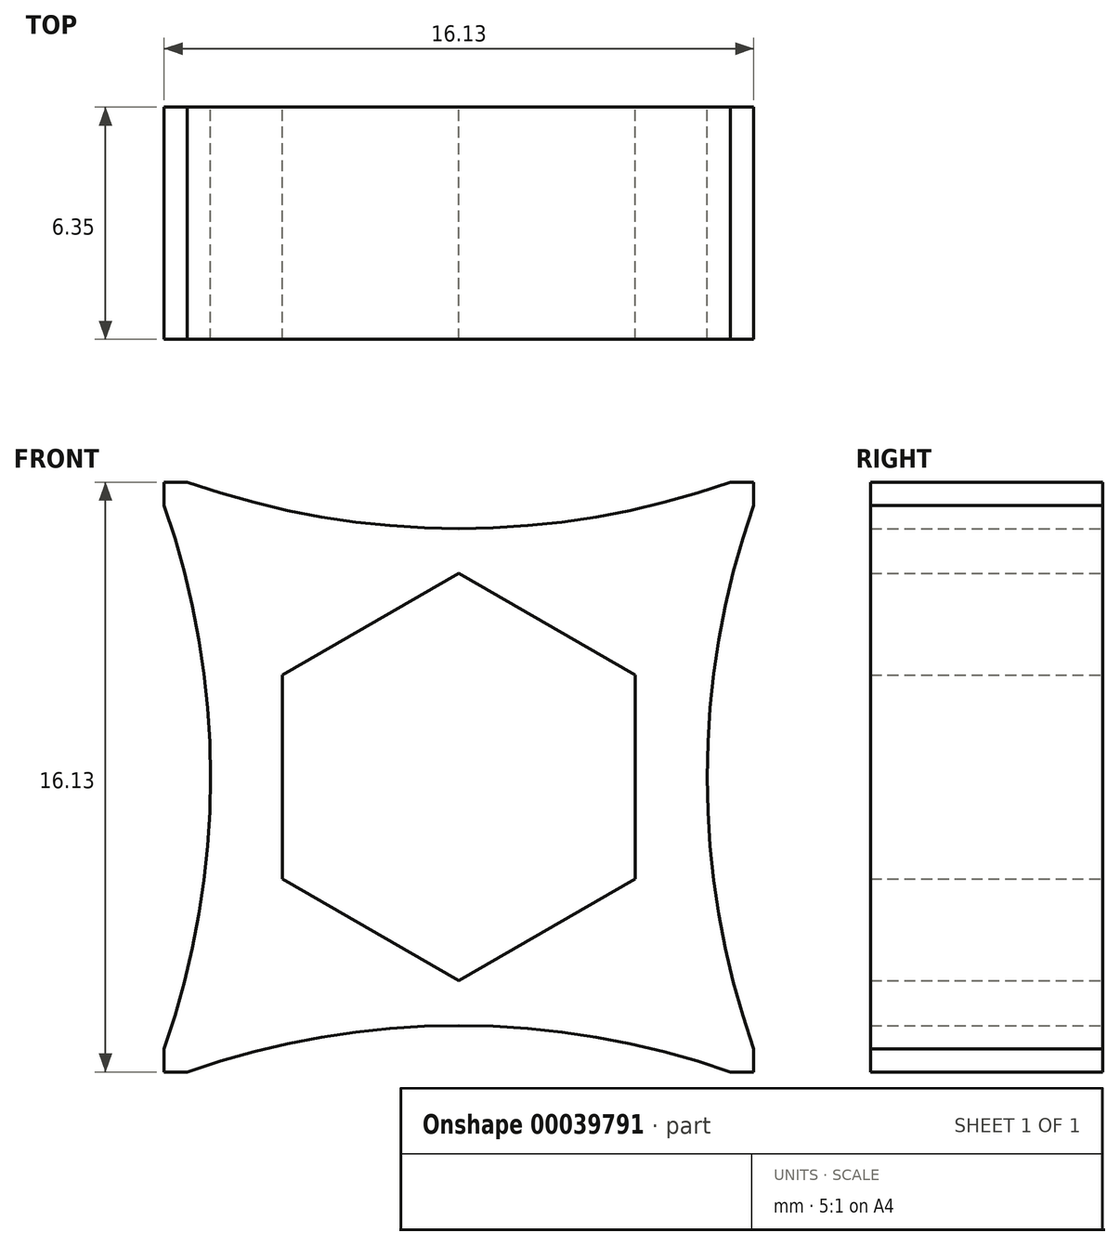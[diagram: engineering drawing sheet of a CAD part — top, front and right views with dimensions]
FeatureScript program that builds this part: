
annotation { "Feature Type Name" : "Feature", "Feature Type Description" : "" }
export const myFeature = defineFeature(function(context is Context, id is Id, definition is map)
    precondition{}
    {
        {
            var Q0;
            Q0=qCreatedBy(makeId("Front.planeOp"),FACE);
            var sketch = newSketch(context, id + "F0", { "sketchPlane" : qUnion([Q0])});
            skLineSegment(sketch, "E0", {"start": v(16.13, 16.13) * mm, "end": v(16.13, 15.5) * mm});
            skLineSegment(sketch, "E1", {"start": v(16.13, 0) * mm, "end": v(16.13, 0.64) * mm});
            skLineSegment(sketch, "E2", {"start": v(16.13, 8.06) * mm, "end": v(14.86, 8.06) * mm, "construction": true});
            skArc(sketch, "E3", {"start": v(16.13, 15.5) * mm, "mid": v(14.86, 8.06) * mm, "end": v(16.13, 0.63) * mm});
            skLineSegment(sketch, "E4", {"start": v(16.13, 16.13) * mm, "end": v(15.5, 16.13) * mm});
            skLineSegment(sketch, "E5", {"start": v(0, 16.13) * mm, "end": v(0.64, 16.13) * mm});
            skLineSegment(sketch, "E6", {"start": v(8.06, 16.13) * mm, "end": v(8.06, 14.86) * mm, "construction": true});
            skArc(sketch, "E7", {"start": v(0.64, 16.13) * mm, "mid": v(8.06, 14.86) * mm, "end": v(15.5, 16.13) * mm});
            skLineSegment(sketch, "E8", {"start": v(0, 16.13) * mm, "end": v(0, 15.5) * mm});
            skLineSegment(sketch, "E9", {"start": v(0, 0) * mm, "end": v(0, 1.27) * mm});
            skLineSegment(sketch, "E10", {"start": v(0, 8.06) * mm, "end": v(1.27, 8.06) * mm, "construction": true});
            skLineSegment(sketch, "E11", {"start": v(0, 0) * mm, "end": v(0, 0.64) * mm});
            skArc(sketch, "E12", {"start": v(0, 0.63) * mm, "mid": v(1.27, 8.06) * mm, "end": v(0, 15.5) * mm});
            skLineSegment(sketch, "E13", {"start": v(0, 0) * mm, "end": v(0.64, 0) * mm});
            skLineSegment(sketch, "E14", {"start": v(16.13, 0) * mm, "end": v(14.86, 0) * mm});
            skLineSegment(sketch, "E15", {"start": v(16.13, 0) * mm, "end": v(15.5, 0) * mm});
            skLineSegment(sketch, "E16", {"start": v(8.06, 0) * mm, "end": v(8.06, 1.27) * mm});
            skArc(sketch, "E17", {"start": v(15.5, 0) * mm, "mid": v(8.06, 1.27) * mm, "end": v(0.63, 0) * mm});
            skLineSegment(sketch, "E18", {"start": v(1.27, 8.06) * mm, "end": v(14.86, 8.06) * mm, "construction": true});
            skLineSegment(sketch, "E19", {"start": v(8.06, 14.86) * mm, "end": v(8.06, 1.27) * mm, "construction": true});
            skLineSegment(sketch, "E20", {"start": v(8.06, 8.06) * mm, "end": v(12.9, 8.06) * mm});
            skCircle(sketch, "E21.cCircle", {"center": v(8.06, 8.06) * mm, "radius": 4.83 * mm, "construction": true});
            skLineSegment(sketch, "E21.0", {"start": v(12.9, 10.85) * mm, "end": v(12.9, 5.28) * mm});
            skLineSegment(sketch, "E21.1", {"start": v(12.9, 5.28) * mm, "end": v(8.06, 2.5) * mm});
            skLineSegment(sketch, "E21.2", {"start": v(8.06, 2.5) * mm, "end": v(3.24, 5.28) * mm});
            skLineSegment(sketch, "E21.3", {"start": v(3.24, 5.28) * mm, "end": v(3.24, 10.85) * mm});
            skLineSegment(sketch, "E21.4", {"start": v(3.24, 10.85) * mm, "end": v(8.06, 13.64) * mm});
            skLineSegment(sketch, "E21.5", {"start": v(8.06, 13.64) * mm, "end": v(12.9, 10.85) * mm});
            skPoint(sketch, "E21.0.midPoint", {"position": v(12.9, 8.06) * mm});
            skLineSegment(sketch, "E22", {"start": v(0, 16.13) * mm, "end": v(0, 0) * mm, "construction": true});
            skSolve(sketch);
        }
        {
            var Q0;
            Q0 = qSketchRegion(id + "F0", true);
            extrude(context, id + "F1", {"entities" : qUnion([Q0]), "depth" : 6.35 * mm});
        }
    });
